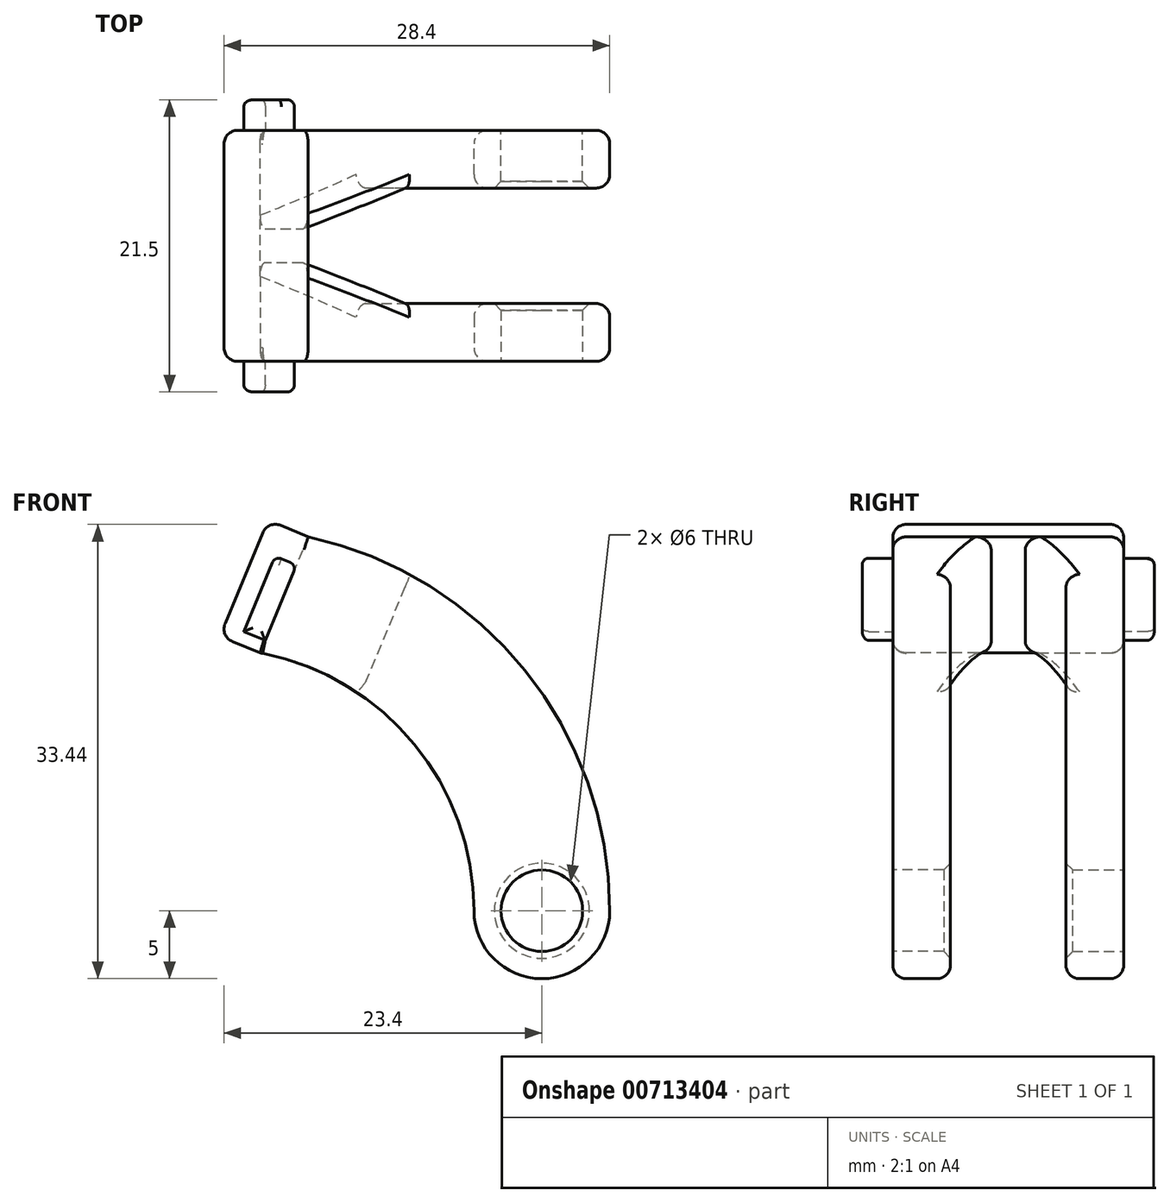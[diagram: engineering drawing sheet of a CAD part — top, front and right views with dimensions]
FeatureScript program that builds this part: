
annotation { "Feature Type Name" : "Feature", "Feature Type Description" : "" }
export const myFeature = defineFeature(function(context is Context, id is Id, definition is map)
    precondition{}
    {
        {
            var Q0;
            Q0=qCreatedBy(makeId("Front.planeOp"),FACE);
            var sketch = newSketch(context, id + "F0", { "sketchPlane" : qUnion([Q0])});
            skLineSegment(sketch, "E0.bottom", {"start": v(0.36, 3.1) * mm, "end": v(1.93, 2.45) * mm});
            skLineSegment(sketch, "E0.top", {"start": v(-1.93, -2.45) * mm, "end": v(-0.36, -3.1) * mm});
            skLineSegment(sketch, "E0.left", {"start": v(0.36, 3.1) * mm, "end": v(-1.93, -2.45) * mm});
            skLineSegment(sketch, "E0.right", {"start": v(1.93, 2.45) * mm, "end": v(-0.36, -3.1) * mm});
            skPoint(sketch, "E0.middle", {"position": v(0, 0) * mm});
            skLineSegment(sketch, "E1", {"start": v(1.93, 2.45) * mm, "end": v(2.8, 4.53) * mm});
            skLineSegment(sketch, "E2", {"start": v(2.8, 4.53) * mm, "end": v(-0.16, 5.75) * mm});
            skLineSegment(sketch, "E3", {"start": v(-0.16, 5.75) * mm, "end": v(-3.7, -2.8) * mm});
            skLineSegment(sketch, "E4", {"start": v(-3.7, -2.8) * mm, "end": v(-0.75, -4.02) * mm});
            skLineSegment(sketch, "E5", {"start": v(-0.75, -4.02) * mm, "end": v(-0.36, -3.1) * mm});
            skArc(sketch, "E6", {"start": v(25, -23) * mm, "mid": v(18.76, -5.32) * mm, "end": v(2.8, 4.53) * mm});
            skCircle(sketch, "E7", {"center": v(20, -23) * mm, "radius": 3 * mm});
            skArc(sketch, "E8", {"start": v(15, -23) * mm, "mid": v(20, -28) * mm, "end": v(25, -23) * mm});
            skArc(sketch, "E9", {"start": v(15, -23) * mm, "mid": v(10.55, -10.67) * mm, "end": v(-0.75, -4.02) * mm});
            skSolve(sketch);
        }
        {
            var Q0;
            Q0=makeQuery(id+"F0.imprint","IMPRINT",FACE,{"disambiguationData":[TD([[makeQuery(id+"F0.imprint","IMPRINT",EDGE,{"derivedFrom":sQuery(id+"F0.wireOp",EDGE,"E0.right")}),1.0]])]});
            var Q1;
            Q1=makeQuery(id+"F0.imprint","IMPRINT",FACE,{"disambiguationData":[TD([[makeQuery(id+"F0.imprint","IMPRINT",EDGE,{"derivedFrom":sQuery(id+"F0.wireOp",EDGE,"E0.bottom")}),-1.0]])]});
            var Q2;
            Q2=makeQuery(id+"F0.imprint","IMPRINT",FACE,{"disambiguationData":[TD([[makeQuery(id+"F0.imprint","IMPRINT",EDGE,{"derivedFrom":sQuery(id+"F0.wireOp",EDGE,"E0.bottom")}),1.0]])]});
            extrude(context, id + "F1", {"entities" : qUnion([Q0, Q1, Q2]), "depth" : 4.25 * mm, "offsetDistance" : 25 * mm});
        }
        {
            var Q0;
            Q0=makeQuery(id+"F0.imprint","IMPRINT",FACE,{"disambiguationData":[TD([[makeQuery(id+"F0.imprint","IMPRINT",EDGE,{"derivedFrom":sQuery(id+"F0.wireOp",EDGE,"E0.bottom")}),1.0]])]});
            var Q1;
            Q1=makeQuery(id+"F0.imprint","IMPRINT",FACE,{"disambiguationData":[TD([[makeQuery(id+"F0.imprint","IMPRINT",EDGE,{"derivedFrom":sQuery(id+"F0.wireOp",EDGE,"E0.bottom")}),-1.0]])]});
            extrude(context, id + "F2", {"entities" : qUnion([Q0, Q1]), "operationType" : NewBodyOperationType.ADD, "depth" : 8.5 * mm, "offsetDistance" : 25 * mm});
        }
        {
            var Q0;
            Q0=makeQuery(id+"F0.imprint","IMPRINT",FACE,{"disambiguationData":[TD([[makeQuery(id+"F0.imprint","IMPRINT",EDGE,{"derivedFrom":sQuery(id+"F0.wireOp",EDGE,"E0.bottom")}),-1.0]])]});
            extrude(context, id + "F3", {"entities" : qUnion([Q0]), "operationType" : NewBodyOperationType.ADD, "oppositeDirection" : true, "depth" : 2.25 * mm, "offsetDistance" : 25 * mm});
        }
        {
            var Q0;
            Q0=makeQuery(id+"F1.opExtrude","SWEPT_BODY",BODY,{"disambiguationData":[OSD([sQuery(id+"F0.wireOp",EDGE,"E2"),sQuery(id+"F0.wireOp",EDGE,"E3"),sQuery(id+"F0.wireOp",EDGE,"E4"),sQuery(id+"F0.wireOp",EDGE,"E6"),sQuery(id+"F0.wireOp",EDGE,"E7"),sQuery(id+"F0.wireOp",EDGE,"E8"),sQuery(id+"F0.wireOp",EDGE,"E9")])]});
            var Q1;
            Q1=makeQuery(id+"F2.opExtrude","CAP_FACE",FACE,{"disambiguationData":[OSD([sQuery(id+"F0.wireOp",EDGE,"E0.right"),sQuery(id+"F0.wireOp",EDGE,"E1"),sQuery(id+"F0.wireOp",EDGE,"E2"),sQuery(id+"F0.wireOp",EDGE,"E3"),sQuery(id+"F0.wireOp",EDGE,"E4"),sQuery(id+"F0.wireOp",EDGE,"E5")])],"isStart":false});
            mirror(context, id + "F4", {"operationType" : NewBodyOperationType.ADD, "entities" : qUnion([Q0]), "mirrorPlane" : qUnion([Q1])});
        }
        {
            var Q0;
            Q0=makeQuery(id+"F2.boolean.opBoolean","INTERSECT",EDGE,{"derivedFrom":[makeQuery(id+"F1.opExtrude","CAP_FACE",FACE,{"disambiguationData":[OSD([sQuery(id+"F0.wireOp",EDGE,"E2"),sQuery(id+"F0.wireOp",EDGE,"E3"),sQuery(id+"F0.wireOp",EDGE,"E4"),sQuery(id+"F0.wireOp",EDGE,"E6"),sQuery(id+"F0.wireOp",EDGE,"E7"),sQuery(id+"F0.wireOp",EDGE,"E8"),sQuery(id+"F0.wireOp",EDGE,"E9")])],"isStart":false}),makeQuery(id+"F2.opExtrude","SWEPT_FACE",FACE,{"disambiguationData":[OSD([sQuery(id+"F0.wireOp",EDGE,"E0.right"),sQuery(id+"F0.wireOp",EDGE,"E1"),sQuery(id+"F0.wireOp",EDGE,"E5")])]})]});
            var Q1;
            Q1=makeQuery(id+"F4.opPattern","COPY",EDGE,{"derivedFrom":makeQuery(id+"F2.boolean.opBoolean","INTERSECT",EDGE,{"derivedFrom":[makeQuery(id+"F1.opExtrude","CAP_FACE",FACE,{"disambiguationData":[OSD([sQuery(id+"F0.wireOp",EDGE,"E2"),sQuery(id+"F0.wireOp",EDGE,"E3"),sQuery(id+"F0.wireOp",EDGE,"E4"),sQuery(id+"F0.wireOp",EDGE,"E6"),sQuery(id+"F0.wireOp",EDGE,"E7"),sQuery(id+"F0.wireOp",EDGE,"E8"),sQuery(id+"F0.wireOp",EDGE,"E9")])],"isStart":false}),makeQuery(id+"F2.opExtrude","SWEPT_FACE",FACE,{"disambiguationData":[OSD([sQuery(id+"F0.wireOp",EDGE,"E0.right"),sQuery(id+"F0.wireOp",EDGE,"E1"),sQuery(id+"F0.wireOp",EDGE,"E5")])]})]}),"instanceName":"1"});
            chamfer(context, id + "F5", {"entities" : qUnion([Q0, Q1]), "chamferType" : ChamferType.TWO_OFFSETS, "width1" : 8 * mm, "oppositeDirection" : false, "width2" : 3 * mm, "tangentPropagation" : true});
        }
        {
            var Q0;
            {var subQ0=sQuery(id+"F0.wireOp",EDGE,"E6");Q0=makeQuery(id+"F5.opChamfer","BLEND_EDGE",EDGE,{"blendedFrom":[makeQuery(id+"F2.boolean.opBoolean","INTERSECT",EDGE,{"derivedFrom":[makeQuery(id+"F1.opExtrude","CAP_FACE",FACE,{"disambiguationData":[OSD([sQuery(id+"F0.wireOp",EDGE,"E2"),sQuery(id+"F0.wireOp",EDGE,"E3"),sQuery(id+"F0.wireOp",EDGE,"E4"),subQ0,sQuery(id+"F0.wireOp",EDGE,"E7"),sQuery(id+"F0.wireOp",EDGE,"E8"),sQuery(id+"F0.wireOp",EDGE,"E9")])],"isStart":false}),makeQuery(id+"F2.opExtrude","SWEPT_FACE",FACE,{"disambiguationData":[OSD([sQuery(id+"F0.wireOp",EDGE,"E0.right"),sQuery(id+"F0.wireOp",EDGE,"E1"),sQuery(id+"F0.wireOp",EDGE,"E5")])]})]}),makeQuery(id+"F1.opExtrude","SWEPT_FACE",FACE,{"disambiguationData":[OSD([subQ0])]})],"blendedInto":[makeQuery(id+"F1.opExtrude","SWEPT_FACE",FACE,{"disambiguationData":[OSD([subQ0])]})]});}
            var Q1;
            Q1=makeQuery(id+"F1.opExtrude","CAP_EDGE",EDGE,{"disambiguationData":[OSD([sQuery(id+"F0.wireOp",EDGE,"E6")])],"isStart":false});
            var Q2;
            {var subQ0=sQuery(id+"F0.wireOp",EDGE,"E9");Q2=makeQuery(id+"F5.opChamfer","BLEND_EDGE",EDGE,{"blendedFrom":[makeQuery(id+"F2.boolean.opBoolean","INTERSECT",EDGE,{"derivedFrom":[makeQuery(id+"F1.opExtrude","CAP_FACE",FACE,{"disambiguationData":[OSD([sQuery(id+"F0.wireOp",EDGE,"E2"),sQuery(id+"F0.wireOp",EDGE,"E3"),sQuery(id+"F0.wireOp",EDGE,"E4"),sQuery(id+"F0.wireOp",EDGE,"E6"),sQuery(id+"F0.wireOp",EDGE,"E7"),sQuery(id+"F0.wireOp",EDGE,"E8"),subQ0])],"isStart":false}),makeQuery(id+"F2.opExtrude","SWEPT_FACE",FACE,{"disambiguationData":[OSD([sQuery(id+"F0.wireOp",EDGE,"E0.right"),sQuery(id+"F0.wireOp",EDGE,"E1"),sQuery(id+"F0.wireOp",EDGE,"E5")])]})]}),makeQuery(id+"F1.opExtrude","SWEPT_FACE",FACE,{"disambiguationData":[OSD([subQ0])]})],"blendedInto":[makeQuery(id+"F1.opExtrude","SWEPT_FACE",FACE,{"disambiguationData":[OSD([subQ0])]})]});}
            var Q3;
            Q3=makeQuery(id+"F1.opExtrude","CAP_EDGE",EDGE,{"disambiguationData":[OSD([sQuery(id+"F0.wireOp",EDGE,"E6")])],"isStart":true});
            var Q4;
            {var subQ0=sQuery(id+"F0.wireOp",EDGE,"E3");var subQ1=sQuery(id+"F0.wireOp",EDGE,"E2");Q4=makeQuery(id+"F2.boolean.opBoolean","MERGE",EDGE,{"derivedFrom":[makeQuery(id+"F1.opExtrude","SWEPT_EDGE",EDGE,{"disambiguationData":[OSD([subQ1,subQ0])]}),makeQuery(id+"F2.opExtrude","SWEPT_EDGE",EDGE,{"disambiguationData":[OSD([subQ1,subQ0])]})]});}
            var Q5;
            Q5=makeQuery(id+"F1.opExtrude","CAP_EDGE",EDGE,{"disambiguationData":[OSD([sQuery(id+"F0.wireOp",EDGE,"E3")])],"isStart":true});
            var Q6;
            {var subQ0=sQuery(id+"F0.wireOp",EDGE,"E4");var subQ1=sQuery(id+"F0.wireOp",EDGE,"E3");Q6=makeQuery(id+"F2.boolean.opBoolean","MERGE",EDGE,{"derivedFrom":[makeQuery(id+"F1.opExtrude","SWEPT_EDGE",EDGE,{"disambiguationData":[OSD([subQ1,subQ0])]}),makeQuery(id+"F2.opExtrude","SWEPT_EDGE",EDGE,{"disambiguationData":[OSD([subQ1,subQ0])]})]});}
            var Q7;
            Q7=makeQuery(id+"F1.opExtrude","CAP_EDGE",EDGE,{"disambiguationData":[OSD([sQuery(id+"F0.wireOp",EDGE,"E4")])],"isStart":true});
            var Q8;
            Q8=makeQuery(id+"F1.opExtrude","CAP_EDGE",EDGE,{"disambiguationData":[OSD([sQuery(id+"F0.wireOp",EDGE,"E2")])],"isStart":true});
            var Q9;
            {var subQ0=sQuery(id+"F0.wireOp",EDGE,"E6");Q9=makeQuery(id+"F5.opChamfer","BLEND_EDGE",EDGE,{"blendedFrom":[makeQuery(id+"F4.opPattern","COPY",EDGE,{"derivedFrom":makeQuery(id+"F2.boolean.opBoolean","INTERSECT",EDGE,{"derivedFrom":[makeQuery(id+"F1.opExtrude","CAP_FACE",FACE,{"disambiguationData":[OSD([sQuery(id+"F0.wireOp",EDGE,"E2"),sQuery(id+"F0.wireOp",EDGE,"E3"),sQuery(id+"F0.wireOp",EDGE,"E4"),subQ0,sQuery(id+"F0.wireOp",EDGE,"E7"),sQuery(id+"F0.wireOp",EDGE,"E8"),sQuery(id+"F0.wireOp",EDGE,"E9")])],"isStart":false}),makeQuery(id+"F2.opExtrude","SWEPT_FACE",FACE,{"disambiguationData":[OSD([sQuery(id+"F0.wireOp",EDGE,"E0.right"),sQuery(id+"F0.wireOp",EDGE,"E1"),sQuery(id+"F0.wireOp",EDGE,"E5")])]})]}),"instanceName":"1"}),makeQuery(id+"F4.opPattern","COPY",FACE,{"derivedFrom":makeQuery(id+"F1.opExtrude","SWEPT_FACE",FACE,{"disambiguationData":[OSD([subQ0])]}),"instanceName":"1"})],"blendedInto":[makeQuery(id+"F4.opPattern","COPY",FACE,{"derivedFrom":makeQuery(id+"F1.opExtrude","SWEPT_FACE",FACE,{"disambiguationData":[OSD([subQ0])]}),"instanceName":"1"})]});}
            var Q10;
            Q10=makeQuery(id+"F4.opPattern","COPY",EDGE,{"derivedFrom":makeQuery(id+"F1.opExtrude","CAP_EDGE",EDGE,{"disambiguationData":[OSD([sQuery(id+"F0.wireOp",EDGE,"E6")])],"isStart":false}),"instanceName":"1"});
            var Q11;
            {var subQ0=sQuery(id+"F0.wireOp",EDGE,"E9");Q11=makeQuery(id+"F5.opChamfer","BLEND_EDGE",EDGE,{"blendedFrom":[makeQuery(id+"F4.opPattern","COPY",EDGE,{"derivedFrom":makeQuery(id+"F2.boolean.opBoolean","INTERSECT",EDGE,{"derivedFrom":[makeQuery(id+"F1.opExtrude","CAP_FACE",FACE,{"disambiguationData":[OSD([sQuery(id+"F0.wireOp",EDGE,"E2"),sQuery(id+"F0.wireOp",EDGE,"E3"),sQuery(id+"F0.wireOp",EDGE,"E4"),sQuery(id+"F0.wireOp",EDGE,"E6"),sQuery(id+"F0.wireOp",EDGE,"E7"),sQuery(id+"F0.wireOp",EDGE,"E8"),subQ0])],"isStart":false}),makeQuery(id+"F2.opExtrude","SWEPT_FACE",FACE,{"disambiguationData":[OSD([sQuery(id+"F0.wireOp",EDGE,"E0.right"),sQuery(id+"F0.wireOp",EDGE,"E1"),sQuery(id+"F0.wireOp",EDGE,"E5")])]})]}),"instanceName":"1"}),makeQuery(id+"F4.opPattern","COPY",FACE,{"derivedFrom":makeQuery(id+"F1.opExtrude","SWEPT_FACE",FACE,{"disambiguationData":[OSD([subQ0])]}),"instanceName":"1"})],"blendedInto":[makeQuery(id+"F4.opPattern","COPY",FACE,{"derivedFrom":makeQuery(id+"F1.opExtrude","SWEPT_FACE",FACE,{"disambiguationData":[OSD([subQ0])]}),"instanceName":"1"})]});}
            var Q12;
            Q12=makeQuery(id+"F4.opPattern","COPY",EDGE,{"derivedFrom":makeQuery(id+"F1.opExtrude","CAP_EDGE",EDGE,{"disambiguationData":[OSD([sQuery(id+"F0.wireOp",EDGE,"E6")])],"isStart":true}),"instanceName":"1"});
            var Q13;
            Q13=makeQuery(id+"F4.opPattern","COPY",EDGE,{"derivedFrom":makeQuery(id+"F1.opExtrude","CAP_EDGE",EDGE,{"disambiguationData":[OSD([sQuery(id+"F0.wireOp",EDGE,"E4")])],"isStart":true}),"instanceName":"1"});
            var Q14;
            Q14=makeQuery(id+"F4.opPattern","COPY",EDGE,{"derivedFrom":makeQuery(id+"F1.opExtrude","CAP_EDGE",EDGE,{"disambiguationData":[OSD([sQuery(id+"F0.wireOp",EDGE,"E3")])],"isStart":true}),"instanceName":"1"});
            var Q15;
            Q15=makeQuery(id+"F4.opPattern","COPY",EDGE,{"derivedFrom":makeQuery(id+"F1.opExtrude","CAP_EDGE",EDGE,{"disambiguationData":[OSD([sQuery(id+"F0.wireOp",EDGE,"E2")])],"isStart":true}),"instanceName":"1"});
            fillet(context, id + "F6", {"entities" : qUnion([Q0, Q1, Q2, Q3, Q4, Q5, Q6, Q7, Q8, Q9, Q10, Q11, Q12, Q13, Q14, Q15]), "tangentPropagation" : true, "radius" : 1 * mm, "defaultsChanged" : false, "vertexSettings" : [], "allowEdgeOverflow" : false});
        }
        {
            var Q0;
            Q0=makeQuery(id+"F4.opPattern","COPY",EDGE,{"derivedFrom":makeQuery(id+"F1.opExtrude","CAP_EDGE",EDGE,{"disambiguationData":[OSD([sQuery(id+"F0.wireOp",EDGE,"E7")])],"isStart":false}),"instanceName":"1"});
            var Q1;
            Q1=makeQuery(id+"F1.opExtrude","CAP_EDGE",EDGE,{"disambiguationData":[OSD([sQuery(id+"F0.wireOp",EDGE,"E7")])],"isStart":false});
            chamfer(context, id + "F7", {"entities" : qUnion([Q0, Q1]), "width" : 0.5 * mm, "tangentPropagation" : true});
        }
        {
            var Q0;
            Q0=makeQuery(id+"F4.opPattern","COPY",FACE,{"derivedFrom":makeQuery(id+"F3.opExtrude","CAP_FACE",FACE,{"disambiguationData":[OSD([sQuery(id+"F0.wireOp",EDGE,"E0.bottom"),sQuery(id+"F0.wireOp",EDGE,"E0.top"),sQuery(id+"F0.wireOp",EDGE,"E0.left"),sQuery(id+"F0.wireOp",EDGE,"E0.right")])],"isStart":false}),"instanceName":"1"});
            var Q1;
            Q1=makeQuery(id+"F4.opPattern","COPY",EDGE,{"derivedFrom":makeQuery(id+"F3.opExtrude","SWEPT_EDGE",EDGE,{"disambiguationData":[OSD([sQuery(id+"F0.wireOp",EDGE,"E0.bottom"),sQuery(id+"F0.wireOp",EDGE,"E0.right"),sQuery(id+"F0.wireOp",EDGE,"E1")])]}),"instanceName":"1"});
            var Q2;
            Q2=makeQuery(id+"F4.opPattern","COPY",EDGE,{"derivedFrom":makeQuery(id+"F3.opExtrude","SWEPT_EDGE",EDGE,{"disambiguationData":[OSD([sQuery(id+"F0.wireOp",EDGE,"E0.bottom"),sQuery(id+"F0.wireOp",EDGE,"E0.left")])]}),"instanceName":"1"});
            var Q3;
            Q3=makeQuery(id+"F3.opExtrude","CAP_FACE",FACE,{"disambiguationData":[OSD([sQuery(id+"F0.wireOp",EDGE,"E0.bottom"),sQuery(id+"F0.wireOp",EDGE,"E0.top"),sQuery(id+"F0.wireOp",EDGE,"E0.left"),sQuery(id+"F0.wireOp",EDGE,"E0.right")])],"isStart":false});
            var Q4;
            Q4=makeQuery(id+"F3.opExtrude","SWEPT_EDGE",EDGE,{"disambiguationData":[OSD([sQuery(id+"F0.wireOp",EDGE,"E0.bottom"),sQuery(id+"F0.wireOp",EDGE,"E0.right"),sQuery(id+"F0.wireOp",EDGE,"E1")])]});
            var Q5;
            Q5=makeQuery(id+"F3.opExtrude","SWEPT_EDGE",EDGE,{"disambiguationData":[OSD([sQuery(id+"F0.wireOp",EDGE,"E0.bottom"),sQuery(id+"F0.wireOp",EDGE,"E0.left")])]});
            fillet(context, id + "F8", {"entities" : qUnion([Q0, Q1, Q2, Q3, Q4, Q5]), "tangentPropagation" : true, "radius" : 0.5 * mm, "defaultsChanged" : false, "vertexSettings" : [], "allowEdgeOverflow" : false});
        }
    });
